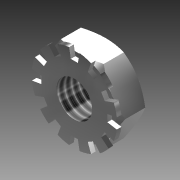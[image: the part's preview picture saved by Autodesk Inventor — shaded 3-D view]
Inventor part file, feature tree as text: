
AUTODESK INVENTOR PART (.ipt)
format: ipt  version: 2013 (Build 170138000, 138)  size: 209,920 bytes
history: native  units: mm (DEFAULTED — no unit token found)
features: sketch x5, extrude x4, revolve x1, plane x1, mirror x1, thread x1, pattern_circular x1
ambient origin geometry x5: Origin, YZ Plane, XZ Plane, XY Plane, Center Point
bodies: Solid1 (feature_tree)
feature tree (14):
  extrude  "Extrusion2"  Depth=8.73252mm
  revolve  "Revolution1"  Angle=90.0deg
  plane  "Work Plane1"
  mirror  "Mirror1"
  extrude  "Extrusion3"  Depth=25.4mm TaperAngle=0.0deg
  thread  "Thread1"  [1 undecoded]
  extrude  "Extrusion5"  TaperAngle=0.0deg  [1 undecoded]
  extrude  "Extrusion6"  Depth=17.453293mm
  pattern_circular  "Circular Pattern1"  [2 undecoded]
  sketch  "Sketch2"  dims[d4=0.0mm d6=8.73252mm]
  sketch  "Sketch4"  dims[d7=30.0deg d8=90.0deg]
  sketch  "Sketch5"  dims[d11=6.35mm d12=0.0mm d13=25.4mm d14=0.0mm d18=10.042398mm]
  sketch  "Sketch7"  dims[d19=0.545548mm d20=0.0mm]
  sketch  "Sketch8"  dims[d21=17.453293mm d22=17.453293mm d23=3.88112mm d24=0.83312mm d25=0.545548mm d26=0.0mm d27=120.0mm d29=360.0deg]
note: 4 required parameter values undecoded (feature->parameter linkage not recoverable at this tier; creation-order binding heuristic only, values carry confidence <= 0.55)
